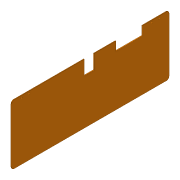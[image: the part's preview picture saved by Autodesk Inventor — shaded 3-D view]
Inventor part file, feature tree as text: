
AUTODESK INVENTOR PART (.ipt)
format: ipt  version: 2016 (Build 200138000, 138)  size: 147,968 bytes
history: native  units: in
note: dims shown in document units (in); Inventor stores cm internally (conversion verified against a paired STEP export)
features: extrude x3, sketch x3, fillet x2
ambient origin geometry x8: Origin, YZ Plane, XZ Plane, XY Plane, X Axis, Y Axis, Z Axis, Center Point
bodies: Body1 (feature_tree)
feature tree (8):
  extrude  "Extrusion2"  Depth=23.7in
  fillet  "Fillet1"  Radius=0.1125in
  fillet  "Fillet2"  Radius=0.4in
  extrude  "Extrusion3"  Depth=0.0225in TaperAngle=0.0deg
  extrude  "Extrusion5"  Depth=4.0in
  sketch  "Sketch1"  dims[d3=9.0in d4=23.7in d5=0.1125in d6=0.0in d7=0.4in]
  sketch  "Sketch3"  dims[d8=0.0225in d19=0.2in d20=0.0in]
  sketch  "Sketch4"  dims[d48=4.0in d49=4.0in d50=0.0in d52=0.2in d53=0.3in d54=1.1in d55=1.5in d58=1.1in d60=1.5in d61=1.1in d62=0.0in d63=0.4477in d64=1.309in d65=1.5in d66=3.25in d67=2.25in d68=0.1in]
